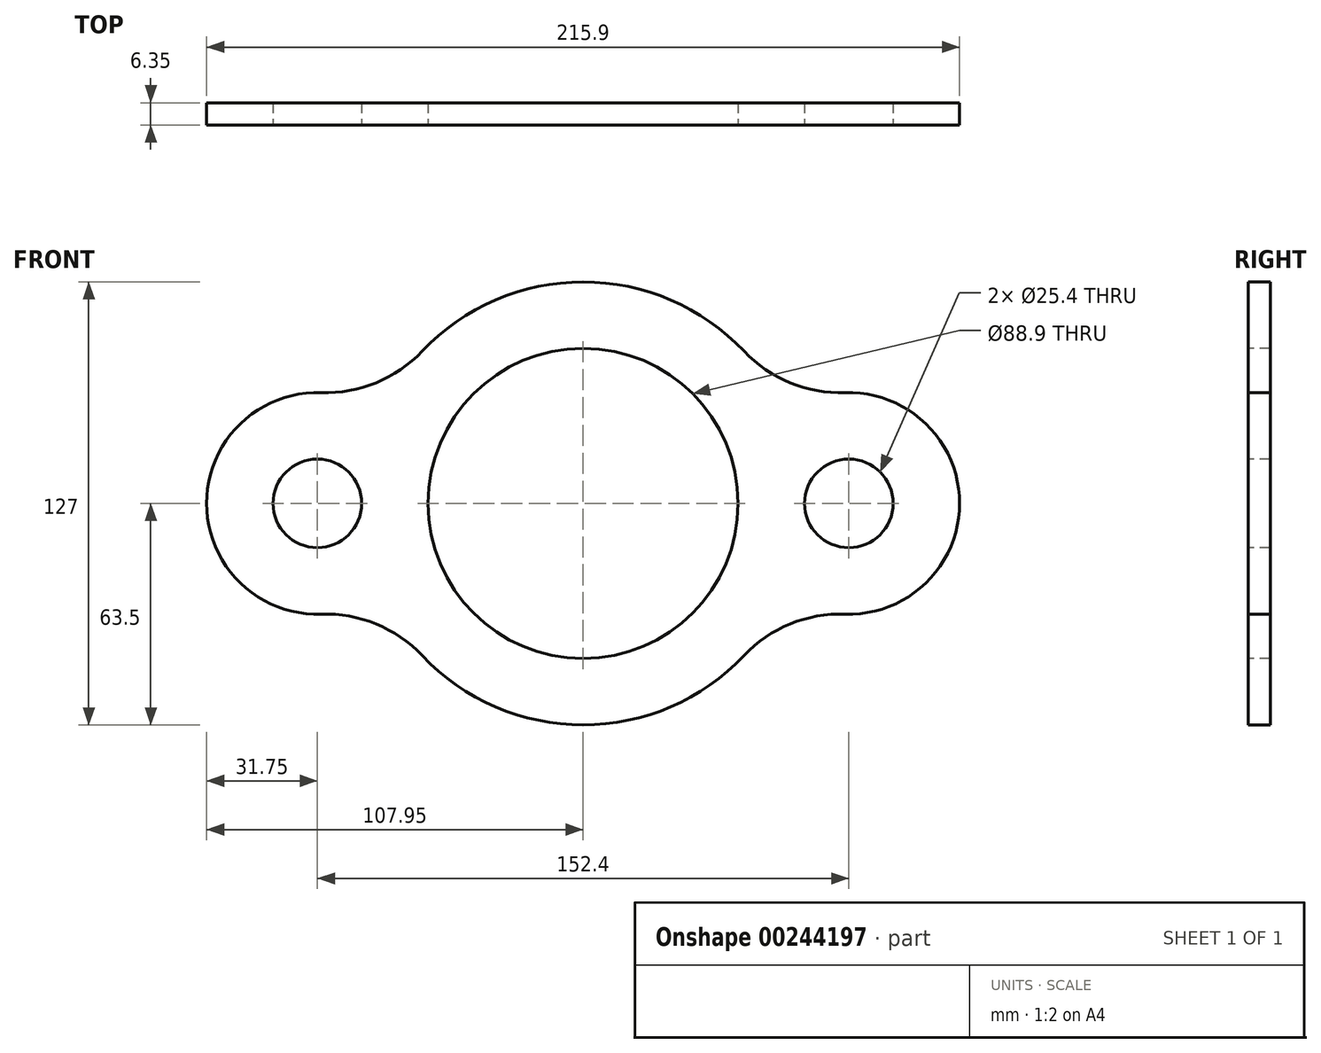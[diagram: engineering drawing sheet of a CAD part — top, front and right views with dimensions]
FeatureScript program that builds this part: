
annotation { "Feature Type Name" : "Feature", "Feature Type Description" : "" }
export const myFeature = defineFeature(function(context is Context, id is Id, definition is map)
    precondition{}
    {
        {
            var Q0;
            Q0=qCreatedBy(makeId("Front.planeOp"),FACE);
            var sketch = newSketch(context, id + "F0", { "sketchPlane" : qUnion([Q0])});
            skArc(sketch, "E0", {"start": v(-46.14, -43.63) * mm, "mid": v(0, -63.5) * mm, "end": v(46.14, -43.63) * mm});
            skCircle(sketch, "E1", {"center": v(0, 0) * mm, "radius": 44.45 * mm});
            skArc(sketch, "E2", {"start": v(75.12, -31.73) * mm, "mid": v(107.95, 0) * mm, "end": v(75.12, 31.73) * mm});
            skCircle(sketch, "E3", {"center": v(76.2, 0) * mm, "radius": 12.7 * mm});
            skArc(sketch, "E4", {"start": v(-75.12, 31.73) * mm, "mid": v(-107.95, 0) * mm, "end": v(-75.12, -31.73) * mm});
            skCircle(sketch, "E5", {"center": v(-76.2, 0) * mm, "radius": 12.7 * mm});
            skArc(sketch, "E6.trimOffspring", {"start": v(46.14, 43.63) * mm, "mid": v(0, 63.5) * mm, "end": v(-46.14, 43.63) * mm});
            skPoint(sketch, "E7.visualSharp", {"position": v(-57.94, 25.98) * mm});
            skArc(sketch, "E7.filletArc", {"start": v(-75.12, 31.73) * mm, "mid": v(-59.35, 34.56) * mm, "end": v(-46.14, 43.63) * mm});
            skPoint(sketch, "E8.visualSharp", {"position": v(57.94, 25.98) * mm});
            skArc(sketch, "E8.filletArc", {"start": v(46.14, 43.63) * mm, "mid": v(59.35, 34.56) * mm, "end": v(75.12, 31.73) * mm});
            skPoint(sketch, "E9.visualSharp", {"position": v(57.94, -25.98) * mm});
            skArc(sketch, "E9.filletArc", {"start": v(75.12, -31.73) * mm, "mid": v(59.35, -34.56) * mm, "end": v(46.14, -43.63) * mm});
            skPoint(sketch, "E10.visualSharp", {"position": v(-57.94, -25.98) * mm});
            skArc(sketch, "E10.filletArc", {"start": v(-46.14, -43.63) * mm, "mid": v(-59.35, -34.56) * mm, "end": v(-75.12, -31.73) * mm});
            skSolve(sketch);
        }
        {
            var Q0;
            Q0 = qSketchRegion(id + "F0", true);
            extrude(context, id + "F1", {"entities" : qUnion([Q0]), "oppositeDirection" : true, "depth" : 6.35 * mm});
        }
    });
